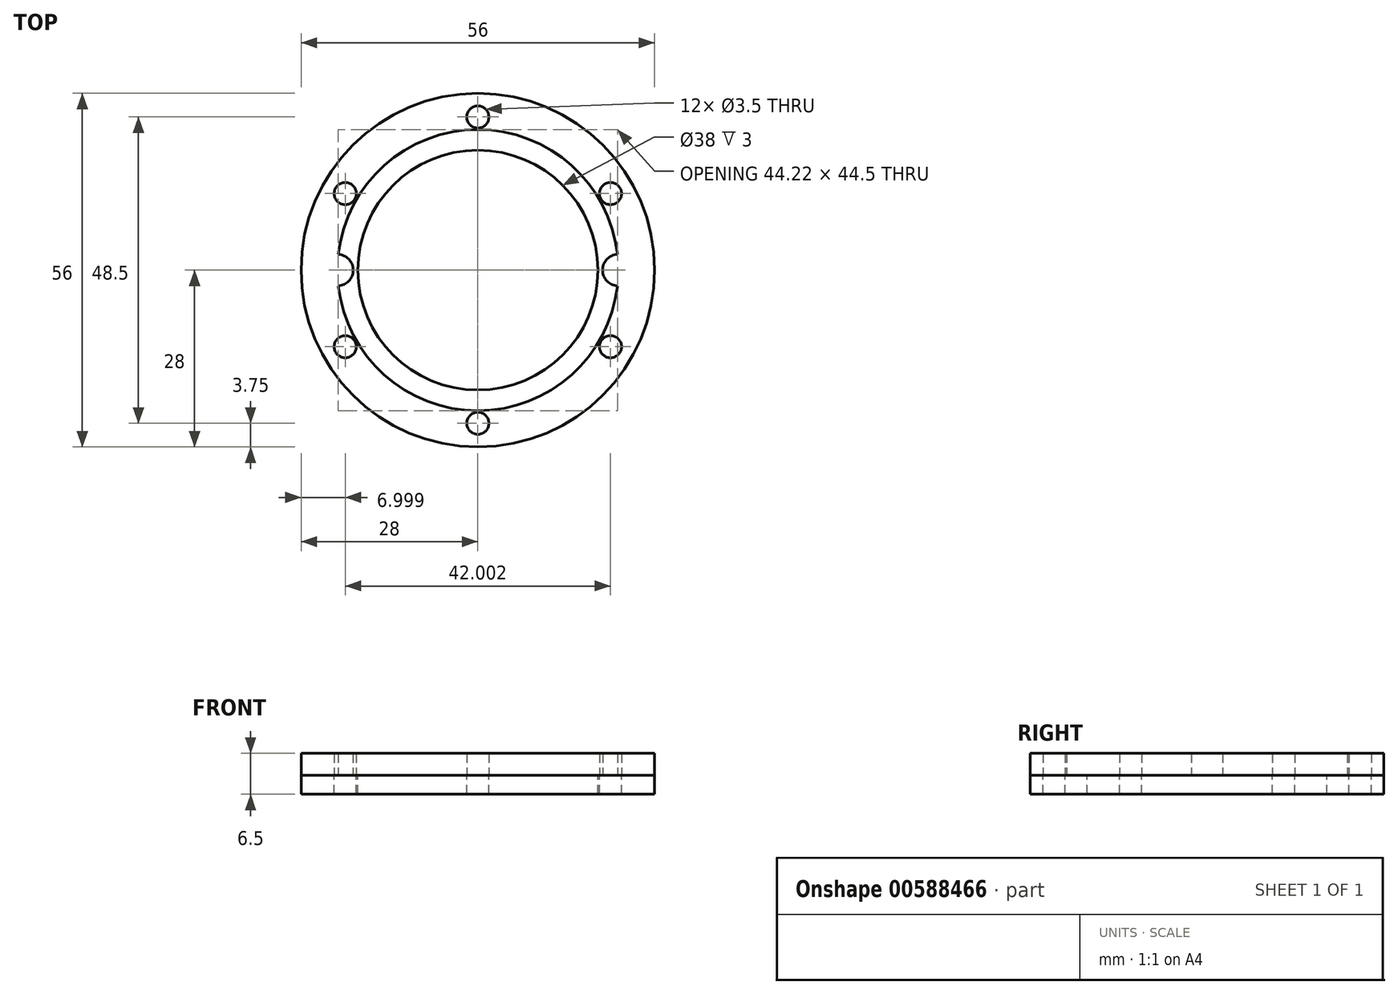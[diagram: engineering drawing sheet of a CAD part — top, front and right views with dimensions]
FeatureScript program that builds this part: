
annotation { "Feature Type Name" : "Feature", "Feature Type Description" : "" }
export const myFeature = defineFeature(function(context is Context, id is Id, definition is map)
    precondition{}
    {
        {
            var Q0;
            Q0=qCreatedBy(makeId("Top.planeOp"),FACE);
            var sketch = newSketch(context, id + "F0", { "sketchPlane" : qUnion([Q0])});
            skCircle(sketch, "E0", {"center": v(0, 0) * mm, "radius": 19 * mm});
            skCircle(sketch, "E1", {"center": v(0, 0) * mm, "radius": 24.25 * mm});
            skCircle(sketch, "E2", {"center": v(0, -24.25) * mm, "radius": 1.75 * mm});
            skCircle(sketch, "E3.1.0", {"center": v(21, -12.13) * mm, "radius": 1.75 * mm});
            skCircle(sketch, "E3.2.0", {"center": v(21, 12.13) * mm, "radius": 1.75 * mm});
            skCircle(sketch, "E4", {"center": v(0, 0) * mm, "radius": 22.25 * mm});
            skCircle(sketch, "E5", {"center": v(22.25, 0) * mm, "radius": 2.5 * mm});
            skCircle(sketch, "E6", {"center": v(-22.25, 0) * mm, "radius": 2.5 * mm});
            skCircle(sketch, "E7", {"center": v(0, 0) * mm, "radius": 28 * mm});
            skCircle(sketch, "E8.1.3.0", {"center": v(0, 24.25) * mm, "radius": 1.75 * mm});
            skCircle(sketch, "E8.1.4.0", {"center": v(-21, 12.13) * mm, "radius": 1.75 * mm});
            skCircle(sketch, "E8.1.5.0", {"center": v(-21, -12.13) * mm, "radius": 1.75 * mm});
            skSolve(sketch);
        }
        {
            var Q0;
            Q0 = qSketchRegion(id + "F0", true);
            var Q1;
            {var subQ1=sQuery(id+"F0.wireOp",EDGE,"E1");var subQ5=sQuery(id+"F0.wireOp",EDGE,"E3.1.0");var subQ6=makeQuery(id+"F0.imprint","INTERSECT",VERTEX,{"disambiguationData":[OD(0.0)],"derivedFrom":[subQ1,subQ5]});Q1=makeQuery(id+"F0.imprint","IMPRINT",FACE,{"disambiguationData":[TD([[makeQuery(id+"F0.imprint","IMPRINT",EDGE,{"disambiguationData":[TD([[subQ6,1.0]])],"derivedFrom":subQ1}),1.0]])]});}
            var Q2;
            {var subQ1=sQuery(id+"F0.wireOp",EDGE,"E1");var subQ4=sQuery(id+"F0.wireOp",EDGE,"E6");var subQ10=makeQuery(id+"F0.imprint","INTERSECT",VERTEX,{"disambiguationData":[OD(1.0)],"derivedFrom":[subQ1,subQ4]});Q2=makeQuery(id+"F0.imprint","IMPRINT",FACE,{"disambiguationData":[TD([[makeQuery(id+"F0.imprint","IMPRINT",EDGE,{"disambiguationData":[TD([[subQ10,-1.0]])],"derivedFrom":subQ1}),1.0]])]});}
            var Q3;
            {var subQ0=sQuery(id+"F0.wireOp",EDGE,"E5");var subQ1=sQuery(id+"F0.wireOp",EDGE,"E4");var subQ2=makeQuery(id+"F0.imprint","INTERSECT",VERTEX,{"disambiguationData":[OD(0.0)],"derivedFrom":[subQ1,subQ0]});Q3=makeQuery(id+"F0.imprint","IMPRINT",FACE,{"disambiguationData":[TD([[makeQuery(id+"F0.imprint","IMPRINT",EDGE,{"disambiguationData":[TD([[subQ2,1.0]])],"derivedFrom":subQ1}),1.0]])]});}
            var Q4;
            {var subQ0=sQuery(id+"F0.wireOp",EDGE,"E5");var subQ1=sQuery(id+"F0.wireOp",EDGE,"E1");var subQ2=makeQuery(id+"F0.imprint","INTERSECT",VERTEX,{"disambiguationData":[OD(0.0)],"derivedFrom":[subQ1,subQ0]});Q4=makeQuery(id+"F0.imprint","IMPRINT",FACE,{"disambiguationData":[TD([[makeQuery(id+"F0.imprint","IMPRINT",EDGE,{"disambiguationData":[TD([[subQ2,1.0]])],"derivedFrom":subQ1}),1.0]])]});}
            var Q5;
            {var subQ0=sQuery(id+"F0.wireOp",EDGE,"E5");var subQ1=sQuery(id+"F0.wireOp",EDGE,"E1");var subQ2=makeQuery(id+"F0.imprint","INTERSECT",VERTEX,{"disambiguationData":[OD(0.0)],"derivedFrom":[subQ1,subQ0]});Q5=makeQuery(id+"F0.imprint","IMPRINT",FACE,{"disambiguationData":[TD([[makeQuery(id+"F0.imprint","IMPRINT",EDGE,{"disambiguationData":[TD([[subQ2,1.0]])],"derivedFrom":subQ1}),-1.0]])]});}
            var Q6;
            {var subQ0=sQuery(id+"F0.wireOp",EDGE,"E6");var subQ1=sQuery(id+"F0.wireOp",EDGE,"E1");var subQ2=makeQuery(id+"F0.imprint","INTERSECT",VERTEX,{"disambiguationData":[OD(0.0)],"derivedFrom":[subQ1,subQ0]});Q6=makeQuery(id+"F0.imprint","IMPRINT",FACE,{"disambiguationData":[TD([[makeQuery(id+"F0.imprint","IMPRINT",EDGE,{"disambiguationData":[TD([[subQ2,-1.0]])],"derivedFrom":subQ1}),-1.0]])]});}
            var Q7;
            {var subQ0=sQuery(id+"F0.wireOp",EDGE,"E6");var subQ1=sQuery(id+"F0.wireOp",EDGE,"E1");var subQ2=makeQuery(id+"F0.imprint","INTERSECT",VERTEX,{"disambiguationData":[OD(0.0)],"derivedFrom":[subQ1,subQ0]});Q7=makeQuery(id+"F0.imprint","IMPRINT",FACE,{"disambiguationData":[TD([[makeQuery(id+"F0.imprint","IMPRINT",EDGE,{"disambiguationData":[TD([[subQ2,-1.0]])],"derivedFrom":subQ1}),1.0]])]});}
            var Q8;
            {var subQ0=sQuery(id+"F0.wireOp",EDGE,"E6");var subQ1=sQuery(id+"F0.wireOp",EDGE,"E4");var subQ2=makeQuery(id+"F0.imprint","INTERSECT",VERTEX,{"disambiguationData":[OD(0.0)],"derivedFrom":[subQ1,subQ0]});Q8=makeQuery(id+"F0.imprint","IMPRINT",FACE,{"disambiguationData":[TD([[makeQuery(id+"F0.imprint","IMPRINT",EDGE,{"disambiguationData":[TD([[subQ2,-1.0]])],"derivedFrom":subQ1}),1.0]])]});}
            var Q9;
            {var subQ1=sQuery(id+"F0.wireOp",EDGE,"E1");var subQ12=sQuery(id+"F0.wireOp",EDGE,"E3.2.0");var subQ15=makeQuery(id+"F0.imprint","INTERSECT",VERTEX,{"disambiguationData":[OD(0.0)],"derivedFrom":[subQ1,subQ12]});Q9=makeQuery(id+"F0.imprint","IMPRINT",FACE,{"disambiguationData":[TD([[makeQuery(id+"F0.imprint","IMPRINT",EDGE,{"disambiguationData":[TD([[subQ15,1.0]])],"derivedFrom":subQ1}),1.0]])]});}
            extrude(context, id + "F1", {"entities" : qUnion([Q0, Q1, Q2, Q3, Q4, Q5, Q6, Q7, Q8, Q9]), "depth" : 3.5 * mm, "offsetDistance" : 25 * mm});
        }
        {
            var Q0;
            Q0 = qSketchRegion(id + "F0", true);
            var Q1;
            {var subQ1=sQuery(id+"F0.wireOp",EDGE,"E1");var subQ4=sQuery(id+"F0.wireOp",EDGE,"E6");var subQ10=makeQuery(id+"F0.imprint","INTERSECT",VERTEX,{"disambiguationData":[OD(1.0)],"derivedFrom":[subQ1,subQ4]});Q1=makeQuery(id+"F0.imprint","IMPRINT",FACE,{"disambiguationData":[TD([[makeQuery(id+"F0.imprint","IMPRINT",EDGE,{"disambiguationData":[TD([[subQ10,-1.0]])],"derivedFrom":subQ1}),1.0]])]});}
            var Q2;
            {var subQ0=sQuery(id+"F0.wireOp",EDGE,"E6");var subQ1=sQuery(id+"F0.wireOp",EDGE,"E1");var subQ2=makeQuery(id+"F0.imprint","INTERSECT",VERTEX,{"disambiguationData":[OD(0.0)],"derivedFrom":[subQ1,subQ0]});Q2=makeQuery(id+"F0.imprint","IMPRINT",FACE,{"disambiguationData":[TD([[makeQuery(id+"F0.imprint","IMPRINT",EDGE,{"disambiguationData":[TD([[subQ2,-1.0]])],"derivedFrom":subQ1}),-1.0]])]});}
            var Q3;
            {var subQ0=sQuery(id+"F0.wireOp",EDGE,"E6");var subQ1=sQuery(id+"F0.wireOp",EDGE,"E1");var subQ2=makeQuery(id+"F0.imprint","INTERSECT",VERTEX,{"disambiguationData":[OD(0.0)],"derivedFrom":[subQ1,subQ0]});Q3=makeQuery(id+"F0.imprint","IMPRINT",FACE,{"disambiguationData":[TD([[makeQuery(id+"F0.imprint","IMPRINT",EDGE,{"disambiguationData":[TD([[subQ2,-1.0]])],"derivedFrom":subQ1}),1.0]])]});}
            var Q4;
            {var subQ0=sQuery(id+"F0.wireOp",EDGE,"E6");var subQ1=sQuery(id+"F0.wireOp",EDGE,"E4");var subQ2=makeQuery(id+"F0.imprint","INTERSECT",VERTEX,{"disambiguationData":[OD(0.0)],"derivedFrom":[subQ1,subQ0]});Q4=makeQuery(id+"F0.imprint","IMPRINT",FACE,{"disambiguationData":[TD([[makeQuery(id+"F0.imprint","IMPRINT",EDGE,{"disambiguationData":[TD([[subQ2,-1.0]])],"derivedFrom":subQ1}),1.0]])]});}
            var Q5;
            Q5=makeQuery(id+"F0.imprint","IMPRINT",FACE,{"disambiguationData":[TD([[makeQuery(id+"F0.imprint","IMPRINT",EDGE,{"derivedFrom":sQuery(id+"F0.wireOp",EDGE,"E0")}),-1.0]])]});
            var Q6;
            {var subQ1=sQuery(id+"F0.wireOp",EDGE,"E1");var subQ5=sQuery(id+"F0.wireOp",EDGE,"E3.1.0");var subQ6=makeQuery(id+"F0.imprint","INTERSECT",VERTEX,{"disambiguationData":[OD(0.0)],"derivedFrom":[subQ1,subQ5]});Q6=makeQuery(id+"F0.imprint","IMPRINT",FACE,{"disambiguationData":[TD([[makeQuery(id+"F0.imprint","IMPRINT",EDGE,{"disambiguationData":[TD([[subQ6,1.0]])],"derivedFrom":subQ1}),1.0]])]});}
            var Q7;
            {var subQ0=sQuery(id+"F0.wireOp",EDGE,"E5");var subQ1=sQuery(id+"F0.wireOp",EDGE,"E1");var subQ2=makeQuery(id+"F0.imprint","INTERSECT",VERTEX,{"disambiguationData":[OD(0.0)],"derivedFrom":[subQ1,subQ0]});Q7=makeQuery(id+"F0.imprint","IMPRINT",FACE,{"disambiguationData":[TD([[makeQuery(id+"F0.imprint","IMPRINT",EDGE,{"disambiguationData":[TD([[subQ2,1.0]])],"derivedFrom":subQ1}),1.0]])]});}
            var Q8;
            {var subQ0=sQuery(id+"F0.wireOp",EDGE,"E5");var subQ1=sQuery(id+"F0.wireOp",EDGE,"E4");var subQ2=makeQuery(id+"F0.imprint","INTERSECT",VERTEX,{"disambiguationData":[OD(0.0)],"derivedFrom":[subQ1,subQ0]});Q8=makeQuery(id+"F0.imprint","IMPRINT",FACE,{"disambiguationData":[TD([[makeQuery(id+"F0.imprint","IMPRINT",EDGE,{"disambiguationData":[TD([[subQ2,1.0]])],"derivedFrom":subQ1}),1.0]])]});}
            var Q9;
            {var subQ0=sQuery(id+"F0.wireOp",EDGE,"E5");var subQ1=sQuery(id+"F0.wireOp",EDGE,"E1");var subQ2=makeQuery(id+"F0.imprint","INTERSECT",VERTEX,{"disambiguationData":[OD(0.0)],"derivedFrom":[subQ1,subQ0]});Q9=makeQuery(id+"F0.imprint","IMPRINT",FACE,{"disambiguationData":[TD([[makeQuery(id+"F0.imprint","IMPRINT",EDGE,{"disambiguationData":[TD([[subQ2,1.0]])],"derivedFrom":subQ1}),-1.0]])]});}
            var Q10;
            {var subQ1=sQuery(id+"F0.wireOp",EDGE,"E1");var subQ12=sQuery(id+"F0.wireOp",EDGE,"E3.2.0");var subQ15=makeQuery(id+"F0.imprint","INTERSECT",VERTEX,{"disambiguationData":[OD(0.0)],"derivedFrom":[subQ1,subQ12]});Q10=makeQuery(id+"F0.imprint","IMPRINT",FACE,{"disambiguationData":[TD([[makeQuery(id+"F0.imprint","IMPRINT",EDGE,{"disambiguationData":[TD([[subQ15,1.0]])],"derivedFrom":subQ1}),1.0]])]});}
            extrude(context, id + "F2", {"entities" : qUnion([Q0, Q1, Q2, Q3, Q4, Q5, Q6, Q7, Q8, Q9, Q10]), "oppositeDirection" : true, "depth" : 3 * mm, "offsetDistance" : 25 * mm});
        }
    });
